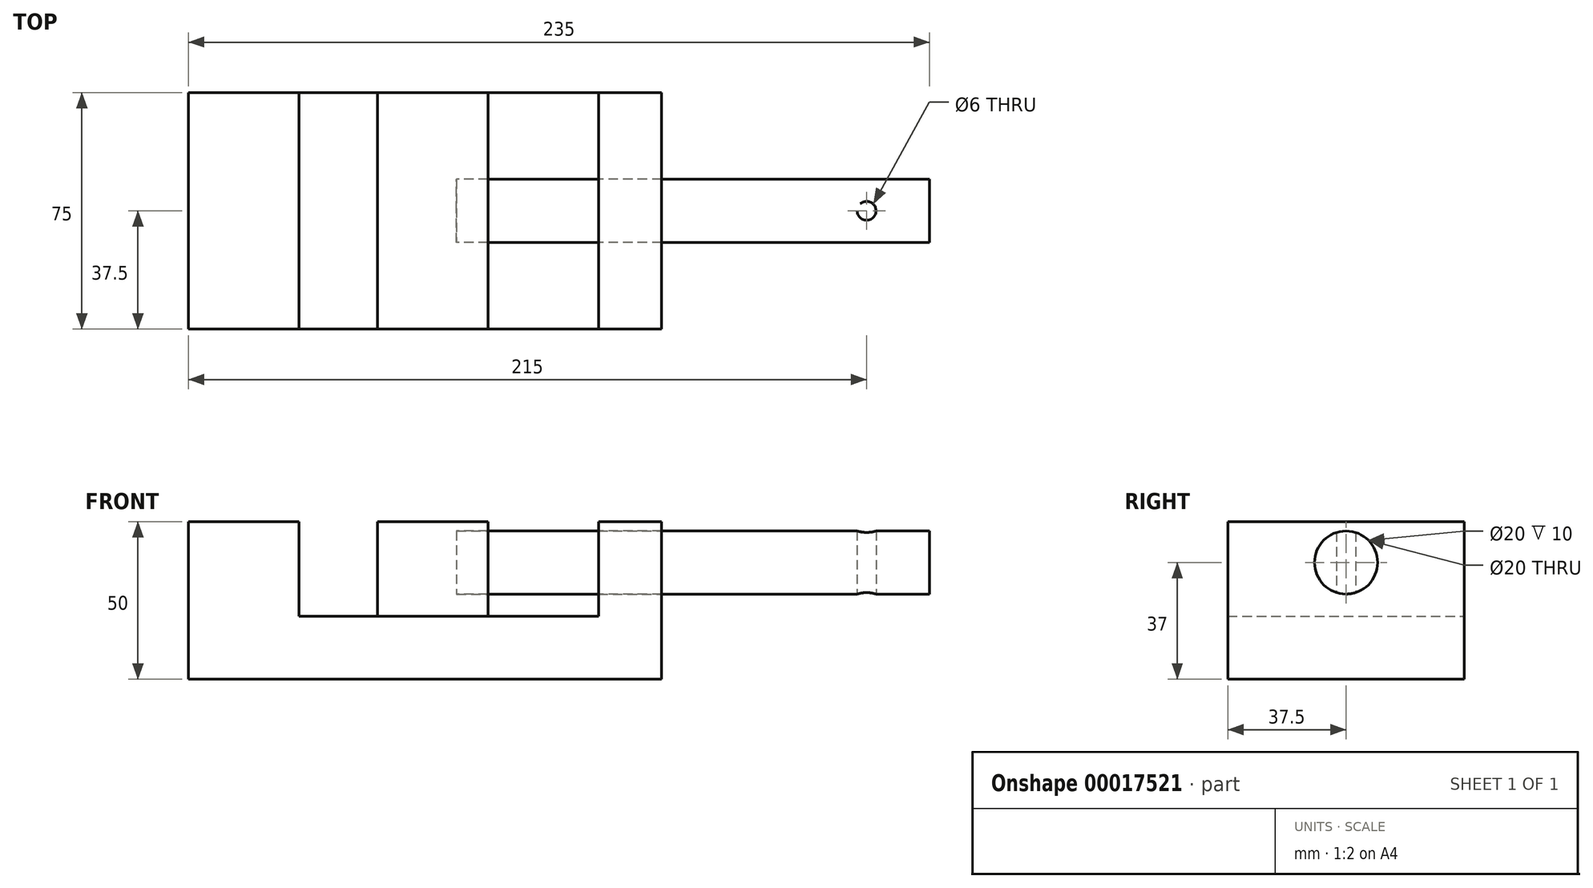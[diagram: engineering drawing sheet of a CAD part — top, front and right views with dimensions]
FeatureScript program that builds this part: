
annotation { "Feature Type Name" : "Feature", "Feature Type Description" : "" }
export const myFeature = defineFeature(function(context is Context, id is Id, definition is map)
    precondition{}
    {
        {
            var Q0;
            Q0=qCreatedBy(makeId("Front.planeOp"),FACE);
            var sketch = newSketch(context, id + "F0", { "sketchPlane" : qUnion([Q0])});
            skLineSegment(sketch, "E0", {"start": v(0, 0) * mm, "end": v(0, 50) * mm});
            skLineSegment(sketch, "E1", {"start": v(0, 50) * mm, "end": v(35, 50) * mm});
            skLineSegment(sketch, "E2", {"start": v(35, 50) * mm, "end": v(35, 20) * mm});
            skLineSegment(sketch, "E3", {"start": v(35, 20) * mm, "end": v(130, 20) * mm});
            skLineSegment(sketch, "E4", {"start": v(130, 20) * mm, "end": v(130, 50) * mm});
            skLineSegment(sketch, "E5", {"start": v(130, 50) * mm, "end": v(150, 50) * mm});
            skLineSegment(sketch, "E6", {"start": v(150, 50) * mm, "end": v(150, 0) * mm});
            skLineSegment(sketch, "E7", {"start": v(150, 0) * mm, "end": v(0, 0) * mm});
            skSolve(sketch);
        }
        {
            var Q0;
            Q0 = qSketchRegion(id + "F0", true);
            extrude(context, id + "F1", {"entities" : qUnion([Q0]), "depth" : 75 * mm, "symmetric" : true});
        }
        {
            var Q0;
            Q0=qCreatedBy(makeId("Front.planeOp"),FACE);
            var sketch = newSketch(context, id + "F2", { "sketchPlane" : qUnion([Q0])});
            skLineSegment(sketch, "E8.bottom", {"start": v(60, 50) * mm, "end": v(95, 50) * mm});
            skLineSegment(sketch, "E8.top", {"start": v(60, 20) * mm, "end": v(95, 20) * mm});
            skLineSegment(sketch, "E8.left", {"start": v(60, 50) * mm, "end": v(60, 20) * mm});
            skLineSegment(sketch, "E8.right", {"start": v(95, 50) * mm, "end": v(95, 20) * mm});
            skSolve(sketch);
        }
        {
            var Q0;
            Q0 = qSketchRegion(id + "F2", true);
            var Q1;
            Q1=makeQuery(id+"F1.opExtrude","CAP_FACE",FACE,{"disambiguationData":[OSD([sQuery(id+"F0.wireOp",EDGE,"E0"),sQuery(id+"F0.wireOp",EDGE,"E1"),sQuery(id+"F0.wireOp",EDGE,"E2"),sQuery(id+"F0.wireOp",EDGE,"E3"),sQuery(id+"F0.wireOp",EDGE,"E4"),sQuery(id+"F0.wireOp",EDGE,"E5"),sQuery(id+"F0.wireOp",EDGE,"E6"),sQuery(id+"F0.wireOp",EDGE,"E7")])],"isStart":false});
            var Q2;
            Q2=makeQuery(id+"F1.opExtrude","CAP_FACE",FACE,{"disambiguationData":[OSD([sQuery(id+"F0.wireOp",EDGE,"E0"),sQuery(id+"F0.wireOp",EDGE,"E1"),sQuery(id+"F0.wireOp",EDGE,"E2"),sQuery(id+"F0.wireOp",EDGE,"E3"),sQuery(id+"F0.wireOp",EDGE,"E4"),sQuery(id+"F0.wireOp",EDGE,"E5"),sQuery(id+"F0.wireOp",EDGE,"E6"),sQuery(id+"F0.wireOp",EDGE,"E7")])],"isStart":true});
            extrude(context, id + "F3", {"entities" : qUnion([Q0]), "endBound" : BoundingType.UP_TO_SURFACE, "endBoundEntityFace" : qUnion([Q1]), "depth" : 25 * mm, "hasSecondDirection" : true, "secondDirectionBound" : BoundingType.UP_TO_SURFACE, "secondDirectionOppositeDirection" : true, "secondDirectionBoundEntityFace" : qUnion([Q2]), "secondDirectionDepth" : 25 * mm});
        }
        {
            var Q0;
            Q0=makeQuery(id+"F1.opExtrude","SWEPT_FACE",FACE,{"disambiguationData":[OSD([sQuery(id+"F0.wireOp",EDGE,"E6")])]});
            var sketch = newSketch(context, id + "F4", { "sketchPlane" : qUnion([Q0])});
            skLineSegment(sketch, "E9.0", {"start": v(-37.5, 20) * mm, "end": v(37.5, 20) * mm});
            skLineSegment(sketch, "E10", {"start": v(0, 20) * mm, "end": v(0, 50) * mm, "construction": true});
            skCircle(sketch, "E11", {"center": v(0, 37) * mm, "radius": 10 * mm});
            skSolve(sketch);
        }
        {
            var Q0;
            Q0 = qSketchRegion(id + "F4", true);
            extrude(context, id + "F5", {"entities" : qUnion([Q0]), "operationType" : NewBodyOperationType.REMOVE, "endBound" : BoundingType.UP_TO_NEXT, "oppositeDirection" : true, "depth" : 25 * mm});
        }
        {
            var Q0;
            Q0=makeQuery(id+"F3.opExtrude","SWEPT_FACE",FACE,{"disambiguationData":[OSD([sQuery(id+"F2.wireOp",EDGE,"E8.right")])]});
            var sketch = newSketch(context, id + "F6", { "sketchPlane" : qUnion([Q0])});
            skCircle(sketch, "E12", {"center": v(0, 37) * mm, "radius": 10 * mm});
            skSolve(sketch);
        }
        {
            var Q0;
            Q0 = qSketchRegion(id + "F6", true);
            extrude(context, id + "F7", {"entities" : qUnion([Q0]), "operationType" : NewBodyOperationType.REMOVE, "oppositeDirection" : true, "depth" : 10 * mm});
        }
        {
            var Q0;
            Q0=qCreatedBy(makeId("Front.planeOp"),FACE);
            var sketch = newSketch(context, id + "F8", { "sketchPlane" : qUnion([Q0])});
            skLineSegment(sketch, "E13.0", {"start": v(150, 47) * mm, "end": v(150, 27) * mm});
            skLineSegment(sketch, "E14.0", {"start": v(85, 47) * mm, "end": v(85, 27) * mm});
            skLineSegment(sketch, "E15", {"start": v(85, 47) * mm, "end": v(235, 47) * mm});
            skLineSegment(sketch, "E16", {"start": v(85, 37) * mm, "end": v(235, 37) * mm});
            skPoint(sketch, "E16.startSnap0", {"position": v(150, 37) * mm});
            skLineSegment(sketch, "E17", {"start": v(235, 47) * mm, "end": v(235, 37) * mm});
            skSolve(sketch);
        }
        {
            var Q0;
            Q0 = qSketchRegion(id + "F8", true);
            var Q1;
            Q1=sQuery(id+"F8.wireOp",EDGE,"E16");
            revolve(context, id + "F9", {"entities" : qUnion([Q0]), "axis" : qUnion([Q1]), "revolveType" : RevolveType.FULL});
        }
        {
            var Q0;
            Q0=qCreatedBy(makeId("Top.planeOp"),FACE);
            var sketch = newSketch(context, id + "F10", { "sketchPlane" : qUnion([Q0])});
            skCircle(sketch, "E18", {"center": v(215, 0) * mm, "radius": 3 * mm});
            skSolve(sketch);
        }
        {
            var Q0;
            Q0 = qSketchRegion(id + "F10", true);
            extrude(context, id + "F11", {"entities" : qUnion([Q0]), "operationType" : NewBodyOperationType.REMOVE, "endBound" : BoundingType.THROUGH_ALL, "depth" : 25 * mm});
        }
    });
